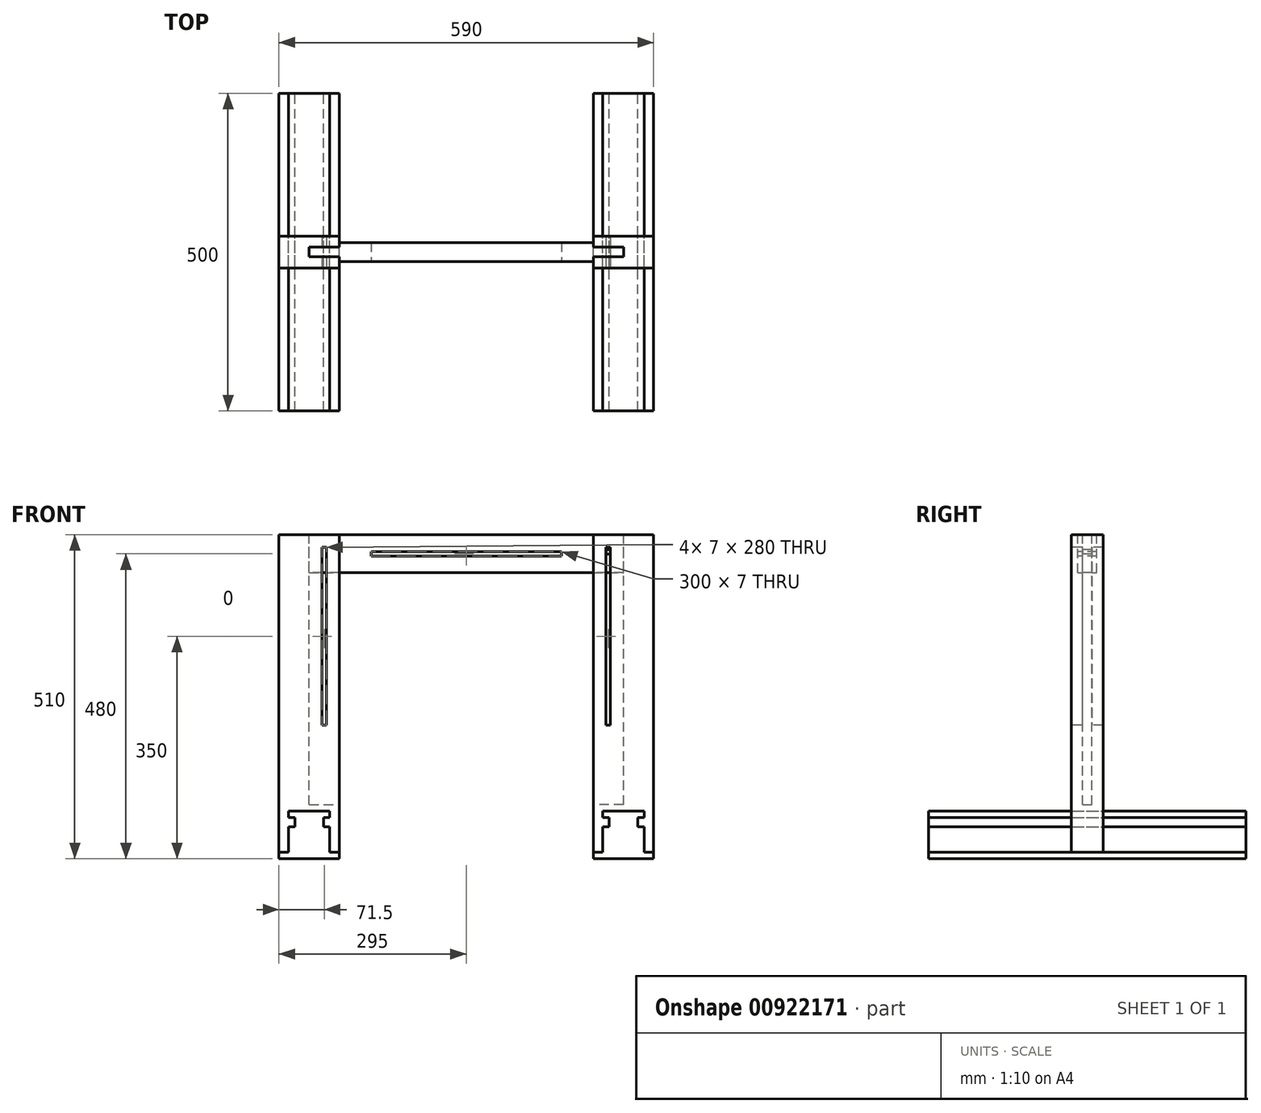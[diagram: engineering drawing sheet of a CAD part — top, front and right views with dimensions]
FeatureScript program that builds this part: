
annotation { "Feature Type Name" : "Feature", "Feature Type Description" : "" }
export const myFeature = defineFeature(function(context is Context, id is Id, definition is map)
    precondition{}
    {
        {
            var Q0;
            Q0=qCreatedBy(makeId("Front.planeOp"),FACE);
            var sketch = newSketch(context, id + "F0", { "sketchPlane" : qUnion([Q0])});
            skLineSegment(sketch, "E0", {"start": v(0, 0) * mm, "end": v(-200, 0) * mm});
            skLineSegment(sketch, "E1", {"start": v(-200, 0) * mm, "end": v(215, 0) * mm});
            skLineSegment(sketch, "E2", {"start": v(215, 0) * mm, "end": v(215, 40) * mm});
            skLineSegment(sketch, "E3", {"start": v(280, 40) * mm, "end": v(280, 0) * mm});
            skLineSegment(sketch, "E4", {"start": v(280, 0) * mm, "end": v(215, 0) * mm});
            skLineSegment(sketch, "E5", {"start": v(0, 0) * mm, "end": v(0, 75.68) * mm, "construction": true});
            skLineSegment(sketch, "E6.MirrorCS", {"start": v(-280, 0) * mm, "end": v(-215, 0) * mm});
            skLineSegment(sketch, "E7.MirrorCS", {"start": v(-215, 0) * mm, "end": v(-215, 40) * mm});
            skLineSegment(sketch, "E8.MirrorCS", {"start": v(-280, 40) * mm, "end": v(-280, 0) * mm});
            skLineSegment(sketch, "E9", {"start": v(215, 0) * mm, "end": v(200, 0) * mm});
            skLineSegment(sketch, "E10", {"start": v(200, 0) * mm, "end": v(200, -10) * mm});
            skLineSegment(sketch, "E11", {"start": v(200, -10) * mm, "end": v(280, -10) * mm});
            skLineSegment(sketch, "E12", {"start": v(280, 0) * mm, "end": v(295, 0) * mm});
            skLineSegment(sketch, "E13", {"start": v(295, 0) * mm, "end": v(295, -10) * mm});
            skLineSegment(sketch, "E14", {"start": v(295, -10) * mm, "end": v(280, -10) * mm});
            skLineSegment(sketch, "E15.MirrorCS", {"start": v(-200, -10) * mm, "end": v(-280, -10) * mm});
            skLineSegment(sketch, "E16.MirrorCS", {"start": v(-295, 0) * mm, "end": v(-295, -10) * mm});
            skLineSegment(sketch, "E17.MirrorCS", {"start": v(-295, -10) * mm, "end": v(-280, -10) * mm});
            skLineSegment(sketch, "E18.MirrorCS", {"start": v(-280, 0) * mm, "end": v(-295, 0) * mm});
            skLineSegment(sketch, "E19.MirrorCS", {"start": v(-215, 0) * mm, "end": v(-200, 0) * mm});
            skLineSegment(sketch, "E20.MirrorCS", {"start": v(-200, 0) * mm, "end": v(-200, -10) * mm});
            skLineSegment(sketch, "E21", {"start": v(215, 40) * mm, "end": v(225, 40) * mm});
            skLineSegment(sketch, "E22", {"start": v(225, 40) * mm, "end": v(225, 55) * mm});
            skLineSegment(sketch, "E23", {"start": v(225, 55) * mm, "end": v(215, 55) * mm});
            skLineSegment(sketch, "E24", {"start": v(215, 55) * mm, "end": v(215, 65) * mm});
            skLineSegment(sketch, "E25", {"start": v(215, 65) * mm, "end": v(280, 65) * mm});
            skLineSegment(sketch, "E26", {"start": v(280, 65) * mm, "end": v(280, 55) * mm});
            skLineSegment(sketch, "E27", {"start": v(280, 55) * mm, "end": v(270, 55) * mm});
            skLineSegment(sketch, "E28", {"start": v(270, 55) * mm, "end": v(270, 40) * mm});
            skLineSegment(sketch, "E29", {"start": v(270, 40) * mm, "end": v(280, 40) * mm});
            skPoint(sketch, "E30.MirrorCS.end.orphan", {"position": v(-280, 40) * mm});
            skPoint(sketch, "E31.MirrorCS.start.orphan", {"position": v(-215, 40) * mm});
            skLineSegment(sketch, "E32.MirrorCS", {"start": v(-215, 40) * mm, "end": v(-225, 40) * mm});
            skLineSegment(sketch, "E33.MirrorCS", {"start": v(-225, 40) * mm, "end": v(-225, 55) * mm});
            skLineSegment(sketch, "E34.MirrorCS", {"start": v(-225, 55) * mm, "end": v(-215, 55) * mm});
            skLineSegment(sketch, "E35.MirrorCS", {"start": v(-215, 55) * mm, "end": v(-215, 65) * mm});
            skLineSegment(sketch, "E36.MirrorCS", {"start": v(-215, 65) * mm, "end": v(-280, 65) * mm});
            skLineSegment(sketch, "E37.MirrorCS", {"start": v(-280, 65) * mm, "end": v(-280, 55) * mm});
            skLineSegment(sketch, "E38.MirrorCS", {"start": v(-280, 55) * mm, "end": v(-270, 55) * mm});
            skLineSegment(sketch, "E39.MirrorCS", {"start": v(-270, 55) * mm, "end": v(-270, 40) * mm});
            skLineSegment(sketch, "E40.MirrorCS", {"start": v(-270, 40) * mm, "end": v(-280, 40) * mm});
            skSolve(sketch);
        }
        {
            var Q0;
            Q0=qSketchRegion(id+"F0",true);
            extrude(context, id + "F1", {"entities" : qUnion([Q0]), "endBound" : BoundingType.SYMMETRIC, "depth" : 500 * mm, "offsetDistance" : 25 * mm});
        }
        {
            var Q0;
            Q0=qCreatedBy(makeId("Front.planeOp"),FACE);
            var sketch = newSketch(context, id + "F2", { "sketchPlane" : qUnion([Q0])});
            skLineSegment(sketch, "E41", {"start": v(-200, 0) * mm, "end": v(-295, 0) * mm});
            skLineSegment(sketch, "E42.0.0", {"start": v(-280, 40) * mm, "end": v(-280, 0) * mm});
            skLineSegment(sketch, "E42.0.1", {"start": v(-280, 0) * mm, "end": v(-295, 0) * mm});
            skLineSegment(sketch, "E42.0.2", {"start": v(-295, 0) * mm, "end": v(-295, 0) * mm});
            skLineSegment(sketch, "E42.0.3", {"start": v(-295, 0) * mm, "end": v(-200, 0) * mm});
            skLineSegment(sketch, "E42.0.4", {"start": v(-200, 0) * mm, "end": v(-200, 0) * mm});
            skLineSegment(sketch, "E42.0.5", {"start": v(-200, 0) * mm, "end": v(-215, 0) * mm});
            skLineSegment(sketch, "E42.0.6", {"start": v(-215, 0) * mm, "end": v(-215, 40) * mm});
            skLineSegment(sketch, "E43.0.0", {"start": v(215, 40) * mm, "end": v(215, 0) * mm});
            skLineSegment(sketch, "E43.0.1", {"start": v(215, 0) * mm, "end": v(200, 0) * mm});
            skLineSegment(sketch, "E43.0.2", {"start": v(200, 0) * mm, "end": v(200, -10) * mm});
            skLineSegment(sketch, "E43.0.3", {"start": v(200, -10) * mm, "end": v(295, -10) * mm});
            skLineSegment(sketch, "E43.0.4", {"start": v(295, -10) * mm, "end": v(295, 0) * mm});
            skLineSegment(sketch, "E43.0.5", {"start": v(295, 0) * mm, "end": v(280, 0) * mm});
            skLineSegment(sketch, "E43.0.6", {"start": v(280, 0) * mm, "end": v(280, 40) * mm});
            skLineSegment(sketch, "E44", {"start": v(-295, 0) * mm, "end": v(-295, 500) * mm});
            skLineSegment(sketch, "E45", {"start": v(-295, 500) * mm, "end": v(-200, 500) * mm});
            skLineSegment(sketch, "E46", {"start": v(-200, 500) * mm, "end": v(-200, 0) * mm});
            skLineSegment(sketch, "E47", {"start": v(0, 0) * mm, "end": v(0, 188.1) * mm, "construction": true});
            skLineSegment(sketch, "E48.0.2", {"start": v(-295, 0) * mm, "end": v(-295, -10) * mm});
            skLineSegment(sketch, "E48.0.3", {"start": v(-295, -10) * mm, "end": v(-200, -10) * mm});
            skLineSegment(sketch, "E48.0.4", {"start": v(-200, -10) * mm, "end": v(-200, 0) * mm});
            skLineSegment(sketch, "E48.0.7", {"start": v(-215, 40) * mm, "end": v(-225, 40) * mm});
            skLineSegment(sketch, "E48.0.8", {"start": v(-225, 40) * mm, "end": v(-225, 55) * mm});
            skLineSegment(sketch, "E48.0.9", {"start": v(-225, 55) * mm, "end": v(-215, 55) * mm});
            skLineSegment(sketch, "E48.0.10", {"start": v(-215, 55) * mm, "end": v(-215, 65) * mm});
            skLineSegment(sketch, "E48.0.11", {"start": v(-215, 65) * mm, "end": v(-280, 65) * mm});
            skLineSegment(sketch, "E48.0.12", {"start": v(-280, 65) * mm, "end": v(-280, 55) * mm});
            skLineSegment(sketch, "E48.0.13", {"start": v(-280, 55) * mm, "end": v(-270, 55) * mm});
            skLineSegment(sketch, "E48.0.14", {"start": v(-270, 55) * mm, "end": v(-270, 40) * mm});
            skLineSegment(sketch, "E48.0.15", {"start": v(-270, 40) * mm, "end": v(-280, 40) * mm});
            skLineSegment(sketch, "E49", {"start": v(0, 0) * mm, "end": v(-200, 0) * mm});
            skSolve(sketch);
        }
        {
            var Q0;
            {var subQ2=sQuery(id+"F2.wireOp",EDGE,"E44");Q0=makeQuery(id+"F2.imprint","IMPRINT",FACE,{"disambiguationData":[TD([[makeQuery(id+"F2.imprint","IMPRINT",EDGE,{"derivedFrom":subQ2}),-1.0]])]});}
            extrude(context, id + "F3", {"entities" : qUnion([Q0]), "endBound" : BoundingType.SYMMETRIC, "depth" : 50 * mm, "offsetDistance" : 25 * mm});
        }
        {
            var Q0;
            Q0=makeQuery(id+"F3.opExtrude","SWEPT_FACE",FACE,{"disambiguationData":[OSD([sQuery(id+"F2.wireOp",EDGE,"E45")])]});
            var sketch = newSketch(context, id + "F4", { "sketchPlane" : qUnion([Q0])});
            skLineSegment(sketch, "E50.0.0", {"start": v(-200, 25) * mm, "end": v(-295, 25) * mm});
            skLineSegment(sketch, "E50.0.1", {"start": v(-295, 25) * mm, "end": v(-295, -25) * mm});
            skLineSegment(sketch, "E50.0.2", {"start": v(-295, -25) * mm, "end": v(-200, -25) * mm});
            skLineSegment(sketch, "E50.0.3", {"start": v(-200, -25) * mm, "end": v(-200, 25) * mm});
            skLineSegment(sketch, "E51", {"start": v(-200, 0) * mm, "end": v(-247.5, 0) * mm});
            skPoint(sketch, "E51.endSnap0", {"position": v(-247.5, -25) * mm});
            skLineSegment(sketch, "E52", {"start": v(-247.5, 0) * mm, "end": v(-247.5, -7.5) * mm});
            skLineSegment(sketch, "E53", {"start": v(-247.5, -7.5) * mm, "end": v(-247.5, 7.5) * mm});
            skLineSegment(sketch, "E54", {"start": v(-247.5, 7.5) * mm, "end": v(-200, 7.5) * mm});
            skLineSegment(sketch, "E55", {"start": v(-200, 7.5) * mm, "end": v(-200, -7.5) * mm});
            skLineSegment(sketch, "E56", {"start": v(-200, -7.5) * mm, "end": v(-247.5, -7.5) * mm});
            skLineSegment(sketch, "E57", {"start": v(-247.5, -25) * mm, "end": v(-200, -25) * mm});
            skSolve(sketch);
        }
        {
            var Q0;
            {var subQ0=sQuery(id+"F4.wireOp",EDGE,"E51");Q0=makeQuery(id+"F4.imprint","IMPRINT",FACE,{"disambiguationData":[TD([[makeQuery(id+"F4.imprint","IMPRINT",EDGE,{"derivedFrom":subQ0}),1.0]])]});}
            var Q1;
            {var subQ0=sQuery(id+"F4.wireOp",EDGE,"E51");Q1=makeQuery(id+"F4.imprint","IMPRINT",FACE,{"disambiguationData":[TD([[makeQuery(id+"F4.imprint","IMPRINT",EDGE,{"derivedFrom":subQ0}),-1.0]])]});}
            extrude(context, id + "F5", {"entities" : qUnion([Q0, Q1]), "operationType" : NewBodyOperationType.REMOVE, "oppositeDirection" : true, "depth" : 425 * mm, "offsetDistance" : 25 * mm});
        }
        {
            var Q0;
            Q0=makeQuery(id+"F3.opExtrude","SWEPT_BODY",BODY,{"disambiguationData":[OSD([sQuery(id+"F2.wireOp",EDGE,"E44"),sQuery(id+"F2.wireOp",EDGE,"E45"),sQuery(id+"F2.wireOp",EDGE,"E46"),sQuery(id+"F2.wireOp",EDGE,"E42.0.0"),sQuery(id+"F2.wireOp",EDGE,"E42.0.1"),sQuery(id+"F2.wireOp",EDGE,"E42.0.5"),sQuery(id+"F2.wireOp",EDGE,"E42.0.6"),sQuery(id+"F2.wireOp",EDGE,"E48.0.7"),sQuery(id+"F2.wireOp",EDGE,"E48.0.8"),sQuery(id+"F2.wireOp",EDGE,"E48.0.9"),sQuery(id+"F2.wireOp",EDGE,"E48.0.10"),sQuery(id+"F2.wireOp",EDGE,"E48.0.11"),sQuery(id+"F2.wireOp",EDGE,"E48.0.12"),sQuery(id+"F2.wireOp",EDGE,"E48.0.13"),sQuery(id+"F2.wireOp",EDGE,"E48.0.14"),sQuery(id+"F2.wireOp",EDGE,"E48.0.15")])]});
            var Q1;
            Q1=qCreatedBy(makeId("Right.planeOp"),FACE);
            mirror(context, id + "F6", {"entities" : qUnion([Q0]), "mirrorPlane" : qUnion([Q1])});
        }
        {
            var Q0;
            Q0=makeQuery(id+"F3.opExtrude","CAP_FACE",FACE,{"disambiguationData":[OSD([sQuery(id+"F2.wireOp",EDGE,"E44"),sQuery(id+"F2.wireOp",EDGE,"E45"),sQuery(id+"F2.wireOp",EDGE,"E46"),sQuery(id+"F2.wireOp",EDGE,"E42.0.0"),sQuery(id+"F2.wireOp",EDGE,"E42.0.1"),sQuery(id+"F2.wireOp",EDGE,"E42.0.5"),sQuery(id+"F2.wireOp",EDGE,"E42.0.6"),sQuery(id+"F2.wireOp",EDGE,"E48.0.7"),sQuery(id+"F2.wireOp",EDGE,"E48.0.8"),sQuery(id+"F2.wireOp",EDGE,"E48.0.9"),sQuery(id+"F2.wireOp",EDGE,"E48.0.10"),sQuery(id+"F2.wireOp",EDGE,"E48.0.11"),sQuery(id+"F2.wireOp",EDGE,"E48.0.12"),sQuery(id+"F2.wireOp",EDGE,"E48.0.13"),sQuery(id+"F2.wireOp",EDGE,"E48.0.14"),sQuery(id+"F2.wireOp",EDGE,"E48.0.15")])],"isStart":false});
            var sketch = newSketch(context, id + "F7", { "sketchPlane" : qUnion([Q0])});
            skLineSegment(sketch, "E58.0.0", {"start": v(-295, 0) * mm, "end": v(-280, 0) * mm});
            skLineSegment(sketch, "E58.0.1", {"start": v(-280, 0) * mm, "end": v(-280, 40) * mm});
            skLineSegment(sketch, "E58.0.2", {"start": v(-280, 40) * mm, "end": v(-270, 40) * mm});
            skLineSegment(sketch, "E58.0.3", {"start": v(-270, 40) * mm, "end": v(-270, 55) * mm});
            skLineSegment(sketch, "E58.0.4", {"start": v(-270, 55) * mm, "end": v(-280, 55) * mm});
            skLineSegment(sketch, "E58.0.5", {"start": v(-280, 55) * mm, "end": v(-280, 65) * mm});
            skLineSegment(sketch, "E58.0.6", {"start": v(-280, 65) * mm, "end": v(-215, 65) * mm});
            skLineSegment(sketch, "E58.0.7", {"start": v(-215, 65) * mm, "end": v(-215, 55) * mm});
            skLineSegment(sketch, "E58.0.8", {"start": v(-215, 55) * mm, "end": v(-225, 55) * mm});
            skLineSegment(sketch, "E58.0.9", {"start": v(-225, 55) * mm, "end": v(-225, 40) * mm});
            skLineSegment(sketch, "E58.0.10", {"start": v(-225, 40) * mm, "end": v(-215, 40) * mm});
            skLineSegment(sketch, "E58.0.11", {"start": v(-215, 40) * mm, "end": v(-215, 0) * mm});
            skLineSegment(sketch, "E58.0.12", {"start": v(-215, 0) * mm, "end": v(-200, 0) * mm});
            skLineSegment(sketch, "E58.0.13", {"start": v(-200, 0) * mm, "end": v(-200, 500) * mm});
            skLineSegment(sketch, "E58.0.14", {"start": v(-200, 500) * mm, "end": v(-295, 500) * mm});
            skLineSegment(sketch, "E58.0.15", {"start": v(-295, 500) * mm, "end": v(-295, 0) * mm});
            skLineSegment(sketch, "E59", {"start": v(-200, 500) * mm, "end": v(-220, 500) * mm});
            skLineSegment(sketch, "E60", {"start": v(-220, 500) * mm, "end": v(-220, 480) * mm});
            skLineSegment(sketch, "E61", {"start": v(-220, 480) * mm, "end": v(-220, 200) * mm});
            skLineSegment(sketch, "E62", {"start": v(-220, 200) * mm, "end": v(-227, 200) * mm});
            skLineSegment(sketch, "E63", {"start": v(-227, 200) * mm, "end": v(-227, 480) * mm});
            skLineSegment(sketch, "E64", {"start": v(-227, 480) * mm, "end": v(-220, 480) * mm});
            skLineSegment(sketch, "E65", {"start": v(0, 0) * mm, "end": v(0, 113.1) * mm, "construction": true});
            skLineSegment(sketch, "E66.MirrorCS", {"start": v(220, 200) * mm, "end": v(227, 200) * mm});
            skLineSegment(sketch, "E67.MirrorCS", {"start": v(227, 200) * mm, "end": v(227, 480) * mm});
            skLineSegment(sketch, "E68.MirrorCS", {"start": v(220, 480) * mm, "end": v(220, 200) * mm});
            skLineSegment(sketch, "E69.MirrorCS", {"start": v(227, 480) * mm, "end": v(220, 480) * mm});
            skSolve(sketch);
        }
        {
            var Q0;
            Q0=makeQuery(id+"F7.imprint","IMPRINT",FACE,{"disambiguationData":[TD([[makeQuery(id+"F7.imprint","IMPRINT",EDGE,{"derivedFrom":sQuery(id+"F7.wireOp",EDGE,"E61")}),-1.0]])]});
            var Q1;
            Q1=makeQuery(id+"F7.imprint","IMPRINT",FACE,{"disambiguationData":[TD([[makeQuery(id+"F7.imprint","IMPRINT",EDGE,{"derivedFrom":sQuery(id+"F7.wireOp",EDGE,"E66.MirrorCS")}),1.0]])]});
            extrude(context, id + "F8", {"entities" : qUnion([Q0, Q1]), "operationType" : NewBodyOperationType.REMOVE, "oppositeDirection" : true, "depth" : 110 * mm, "offsetDistance" : 25 * mm});
        }
        {
            var Q0;
            Q0=makeQuery(id+"F3.opExtrude","SWEPT_FACE",FACE,{"disambiguationData":[OSD([sQuery(id+"F2.wireOp",EDGE,"E45")])]});
            var sketch = newSketch(context, id + "F9", { "sketchPlane" : qUnion([Q0])});
            skLineSegment(sketch, "E70", {"start": v(-200, -25) * mm, "end": v(-200, -7.5) * mm});
            skLineSegment(sketch, "E71", {"start": v(-200, -7.5) * mm, "end": v(-247.5, -7.5) * mm});
            skLineSegment(sketch, "E72", {"start": v(-247.5, -7.5) * mm, "end": v(-247.5, 7.5) * mm});
            skLineSegment(sketch, "E73", {"start": v(-247.5, 7.5) * mm, "end": v(-200, 7.5) * mm});
            skLineSegment(sketch, "E74", {"start": v(-200, 7.5) * mm, "end": v(-200, 25) * mm});
            skLineSegment(sketch, "E75.0.0", {"start": v(200, -7.5) * mm, "end": v(200, -15) * mm});
            skLineSegment(sketch, "E75.0.4", {"start": v(200, 15) * mm, "end": v(200, 7.5) * mm});
            skLineSegment(sketch, "E75.0.5", {"start": v(200, 7.5) * mm, "end": v(247.5, 7.5) * mm});
            skLineSegment(sketch, "E75.0.6", {"start": v(247.5, 7.5) * mm, "end": v(247.5, -7.5) * mm});
            skLineSegment(sketch, "E75.0.7", {"start": v(247.5, -7.5) * mm, "end": v(200, -7.5) * mm});
            skPoint(sketch, "E75.0.2.end.orphan", {"position": v(295, 25) * mm});
            skPoint(sketch, "E75.0.1.end.orphan", {"position": v(295, -25) * mm});
            skLineSegment(sketch, "E76", {"start": v(0, 0) * mm, "end": v(0, -15) * mm, "construction": true});
            skLineSegment(sketch, "E77", {"start": v(0, -15) * mm, "end": v(-200, -15) * mm});
            skLineSegment(sketch, "E78", {"start": v(-200, -15) * mm, "end": v(-200, -7.5) * mm});
            skLineSegment(sketch, "E79", {"start": v(0, 0) * mm, "end": v(0, 15) * mm, "construction": true});
            skLineSegment(sketch, "E80", {"start": v(0, 15) * mm, "end": v(-200, 15) * mm});
            skLineSegment(sketch, "E81", {"start": v(0, 15) * mm, "end": v(200, 15) * mm});
            skLineSegment(sketch, "E82", {"start": v(200, -15) * mm, "end": v(0, -15) * mm});
            skSolve(sketch);
        }
        {
            var Q0;
            Q0=makeQuery(id+"F9.imprint","IMPRINT",FACE,{"disambiguationData":[TD([[makeQuery(id+"F9.imprint","IMPRINT",EDGE,{"derivedFrom":sQuery(id+"F9.wireOp",EDGE,"E71")}),-1.0]])]});
            extrude(context, id + "F10", {"entities" : qUnion([Q0]), "oppositeDirection" : true, "depth" : 60 * mm, "offsetDistance" : 25 * mm});
        }
        {
            var Q0;
            Q0=makeQuery(id+"F10.opExtrude","SWEPT_FACE",FACE,{"disambiguationData":[OSD([sQuery(id+"F9.wireOp",EDGE,"E75.0.5")])]});
            var sketch = newSketch(context, id + "F11", { "sketchPlane" : qUnion([Q0])});
            skLineSegment(sketch, "E83.0.0", {"start": v(-200, 500) * mm, "end": v(-247.5, 500) * mm});
            skLineSegment(sketch, "E83.0.1", {"start": v(-247.5, 500) * mm, "end": v(-247.5, 440) * mm});
            skLineSegment(sketch, "E83.0.2", {"start": v(-247.5, 440) * mm, "end": v(-200, 440) * mm});
            skLineSegment(sketch, "E83.0.3", {"start": v(-200, 440) * mm, "end": v(-200, 500) * mm});
            skLineSegment(sketch, "E84", {"start": v(0, 0) * mm, "end": v(0, 185.23) * mm, "construction": true});
            skLineSegment(sketch, "E85.0", {"start": v(-227, 480) * mm, "end": v(-220, 480) * mm});
            skLineSegment(sketch, "E86", {"start": v(-200, 500) * mm, "end": v(-227, 500) * mm});
            skLineSegment(sketch, "E87", {"start": v(-227, 500) * mm, "end": v(-220, 500) * mm});
            skLineSegment(sketch, "E88", {"start": v(-220, 480) * mm, "end": v(-200, 480) * mm});
            skPoint(sketch, "E89.orphan", {"position": v(-223.75, 440) * mm});
            skLineSegment(sketch, "E90", {"start": v(-220, 480) * mm, "end": v(-227, 480) * mm});
            skLineSegment(sketch, "E91", {"start": v(-223.5, 480) * mm, "end": v(-223.5, 473) * mm});
            skCircle(sketch, "E92", {"center": v(-223.5, 473) * mm, "radius": 3.5 * mm});
            skCircle(sketch, "E93.MirrorC", {"center": v(223.5, 473) * mm, "radius": 3.5 * mm});
            skSolve(sketch);
        }
        {
            var Q0;
            Q0=makeQuery(id+"F11.imprint","IMPRINT",FACE,{"disambiguationData":[TD([[makeQuery(id+"F11.imprint","IMPRINT",EDGE,{"derivedFrom":sQuery(id+"F11.wireOp",EDGE,"E92")}),1.0]])]});
            var Q1;
            Q1=makeQuery(id+"F11.imprint","IMPRINT",FACE,{"disambiguationData":[TD([[makeQuery(id+"F11.imprint","IMPRINT",EDGE,{"derivedFrom":sQuery(id+"F11.wireOp",EDGE,"E93.MirrorC")}),-1.0]])]});
            extrude(context, id + "F12", {"entities" : qUnion([Q0, Q1]), "operationType" : NewBodyOperationType.REMOVE, "endBound" : BoundingType.SYMMETRIC, "depth" : 112 * mm, "offsetDistance" : 25 * mm});
        }
        {
            var Q0;
            Q0=makeQuery(id+"F10.opExtrude","SWEPT_FACE",FACE,{"disambiguationData":[OSD([sQuery(id+"F9.wireOp",EDGE,"E77"),sQuery(id+"F9.wireOp",EDGE,"E82")])]});
            var sketch = newSketch(context, id + "F13", { "sketchPlane" : qUnion([Q0])});
            skLineSegment(sketch, "E94.0.0", {"start": v(200, 500) * mm, "end": v(-200, 500) * mm});
            skLineSegment(sketch, "E94.0.1", {"start": v(-200, 500) * mm, "end": v(-200, 440) * mm});
            skLineSegment(sketch, "E94.0.2", {"start": v(-200, 440) * mm, "end": v(200, 440) * mm});
            skLineSegment(sketch, "E94.0.3", {"start": v(200, 440) * mm, "end": v(200, 500) * mm});
            skLineSegment(sketch, "E95", {"start": v(0, 500) * mm, "end": v(0, 440) * mm, "construction": true});
            skLineSegment(sketch, "E96", {"start": v(0, 470) * mm, "end": v(-150, 470) * mm, "construction": true});
            skLineSegment(sketch, "E97.0", {"start": v(-227, 480) * mm, "end": v(-220, 480) * mm});
            skLineSegment(sketch, "E98", {"start": v(-150, 470) * mm, "end": v(-150, 466.5) * mm});
            skLineSegment(sketch, "E99", {"start": v(-150, 466.5) * mm, "end": v(-150, 473.5) * mm});
            skLineSegment(sketch, "E100", {"start": v(-150, 473.5) * mm, "end": v(0, 473.5) * mm});
            skLineSegment(sketch, "E101", {"start": v(-150, 466.5) * mm, "end": v(0, 466.5) * mm});
            skLineSegment(sketch, "E102.MirrorCS", {"start": v(150, 466.5) * mm, "end": v(0, 466.5) * mm});
            skLineSegment(sketch, "E103.MirrorCS", {"start": v(150, 473.5) * mm, "end": v(0, 473.5) * mm});
            skLineSegment(sketch, "E104.MirrorCS", {"start": v(150, 466.5) * mm, "end": v(150, 473.5) * mm});
            skSolve(sketch);
        }
        {
            var Q0;
            {var subQ1=sQuery(id+"F13.wireOp",EDGE,"E100");Q0=makeQuery(id+"F13.imprint","IMPRINT",FACE,{"disambiguationData":[TD([[makeQuery(id+"F13.imprint","IMPRINT",EDGE,{"derivedFrom":subQ1}),-1.0]])]});}
            extrude(context, id + "F14", {"entities" : qUnion([Q0]), "operationType" : NewBodyOperationType.REMOVE, "oppositeDirection" : true, "depth" : 46 * mm, "offsetDistance" : 25 * mm});
        }
    });
